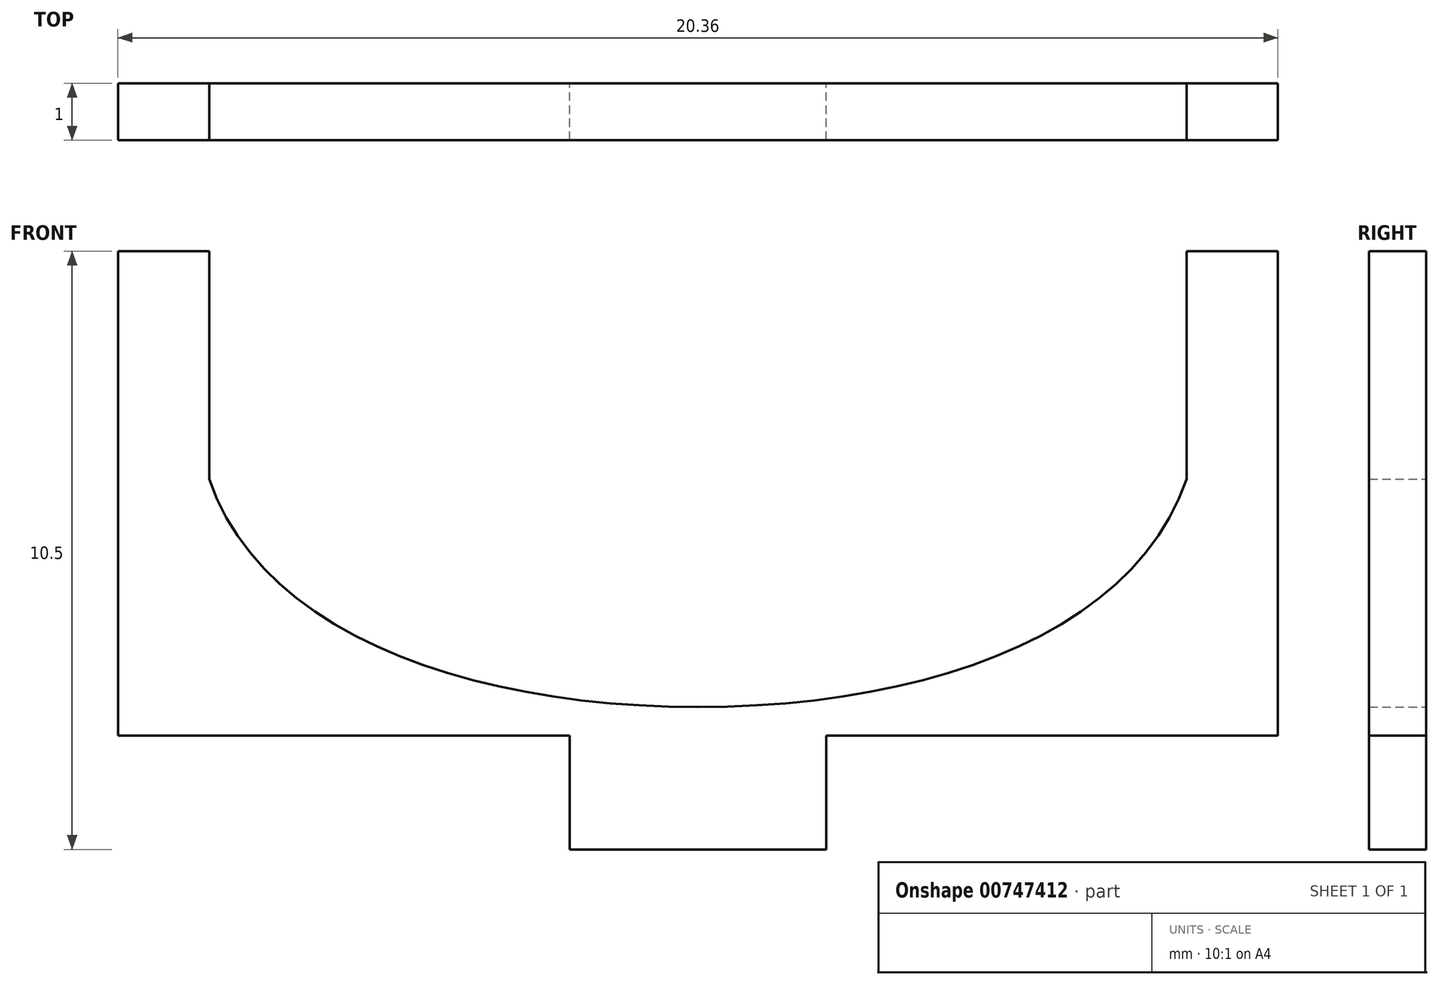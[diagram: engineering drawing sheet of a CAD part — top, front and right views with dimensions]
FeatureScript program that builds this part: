
annotation { "Feature Type Name" : "Feature", "Feature Type Description" : "" }
export const myFeature = defineFeature(function(context is Context, id is Id, definition is map)
    precondition{}
    {
        {
            var Q0;
            Q0=qCreatedBy(makeId("Front.planeOp"),FACE);
            var sketch = newSketch(context, id + "F0", { "sketchPlane" : qUnion([Q0])});
            skFitSpline(sketch, "E0", {"points": [v(0, -4) * mm, v(-8.65, 0.25) * mm], "startDerivative": vector(-12.34, 0) * mm, "endDerivative": vector(-2.33, 8.7) * mm});
            skFitSpline(sketch, "E1.MirrorCS", {"points": [v(0, -4) * mm, v(8.65, 0.25) * mm], "startDerivative": vector(12.34, 0) * mm, "endDerivative": vector(2.33, 8.7) * mm});
            skLineSegment(sketch, "E2", {"start": v(-8.57, 0) * mm, "end": v(8.57, 0) * mm, "construction": true});
            skLineSegment(sketch, "E3", {"start": v(8.57, 4) * mm, "end": v(8.57, 0) * mm});
            skLineSegment(sketch, "E4", {"start": v(-8.57, 0) * mm, "end": v(-8.57, 4) * mm});
            skLineSegment(sketch, "E5", {"start": v(0, 0) * mm, "end": v(0, -4) * mm, "construction": true});
            skLineSegment(sketch, "E6", {"start": v(-8.65, 0.25) * mm, "end": v(-9.2, 2.04) * mm, "construction": true});
            skLineSegment(sketch, "E7", {"start": v(8.65, 0.25) * mm, "end": v(9.28, 2.32) * mm, "construction": true});
            skPoint(sketch, "E8.end.orphan", {"position": v(8.57, 5) * mm});
            skLineSegment(sketch, "E9", {"start": v(-8.57, 4) * mm, "end": v(-10.18, 4) * mm});
            skLineSegment(sketch, "E10", {"start": v(-10.18, 4) * mm, "end": v(-10.18, -4.5) * mm});
            skLineSegment(sketch, "E11", {"start": v(-10.18, -4.5) * mm, "end": v(-2.25, -4.5) * mm});
            skLineSegment(sketch, "E12", {"start": v(10.18, -4.5) * mm, "end": v(10.18, 4) * mm});
            skLineSegment(sketch, "E13", {"start": v(8.57, 4) * mm, "end": v(10.18, 4) * mm});
            skLineSegment(sketch, "E14", {"start": v(-2.25, -4.5) * mm, "end": v(-2.25, -6.5) * mm});
            skLineSegment(sketch, "E15", {"start": v(-2.25, -6.5) * mm, "end": v(2.25, -6.5) * mm});
            skLineSegment(sketch, "E16", {"start": v(2.25, -6.5) * mm, "end": v(2.25, -4.5) * mm});
            skLineSegment(sketch, "E17.trimOffspring", {"start": v(2.25, -4.5) * mm, "end": v(10.18, -4.5) * mm});
            skSolve(sketch);
        }
        {
            var Q0;
            Q0 = qSketchRegion(id + "F0", true);
            extrude(context, id + "F1", {"entities" : qUnion([Q0]), "depth" : 1 * mm, "offsetDistance" : 25 * mm});
        }
    });
